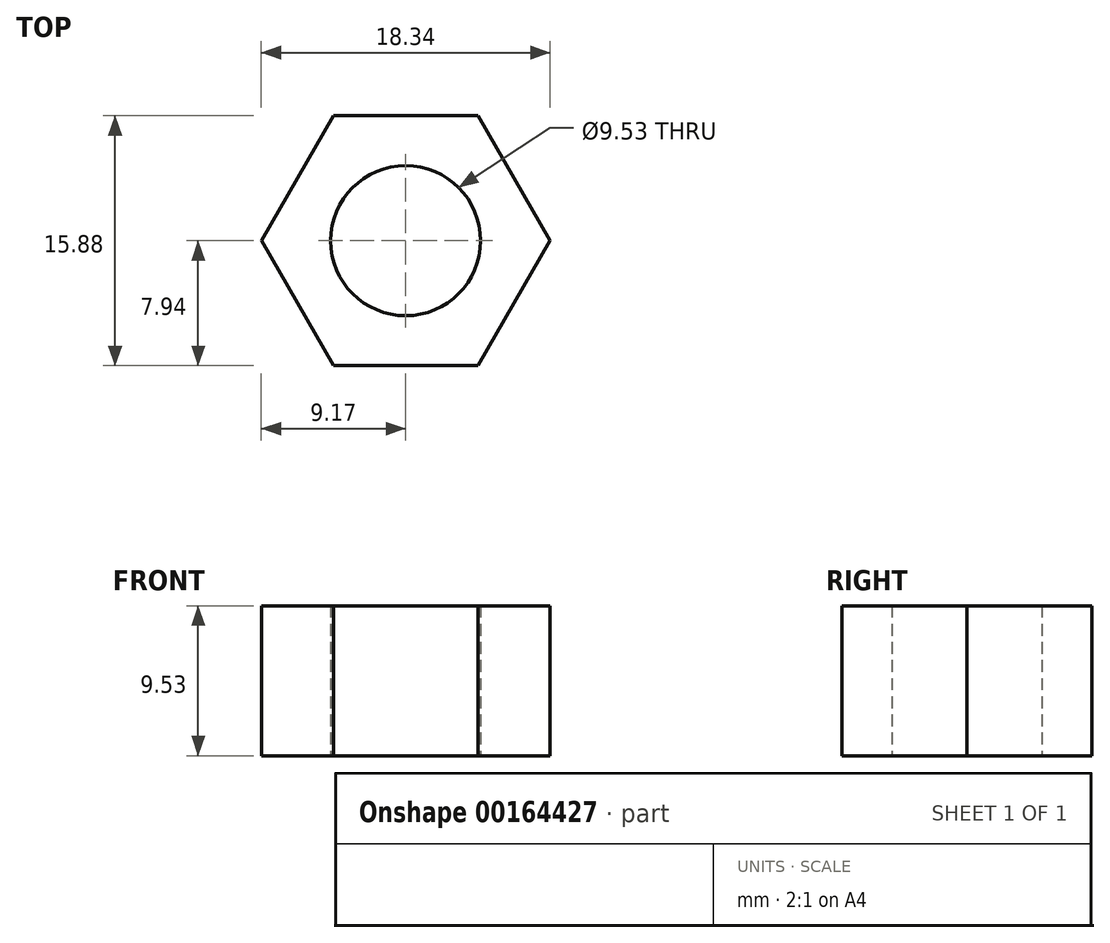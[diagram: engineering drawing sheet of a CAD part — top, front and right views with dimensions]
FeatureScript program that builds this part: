
annotation { "Feature Type Name" : "Feature", "Feature Type Description" : "" }
export const myFeature = defineFeature(function(context is Context, id is Id, definition is map)
    precondition{}
    {
        {
            var Q0;
            Q0=qCreatedBy(makeId("Top.planeOp"),FACE);
            var sketch = newSketch(context, id + "F0", { "sketchPlane" : qUnion([Q0])});
            skCircle(sketch, "E0.cCircle", {"center": v(0, 0) * mm, "radius": 7.94 * mm, "construction": true});
            skLineSegment(sketch, "E0.0", {"start": v(-4.58, -7.94) * mm, "end": v(-9.17, 0) * mm});
            skLineSegment(sketch, "E0.1", {"start": v(-9.17, 0) * mm, "end": v(-4.58, 7.94) * mm});
            skLineSegment(sketch, "E0.2", {"start": v(-4.58, 7.94) * mm, "end": v(4.58, 7.94) * mm});
            skLineSegment(sketch, "E0.3", {"start": v(4.58, 7.94) * mm, "end": v(9.17, 0) * mm});
            skLineSegment(sketch, "E0.4", {"start": v(9.17, 0) * mm, "end": v(4.58, -7.94) * mm});
            skLineSegment(sketch, "E0.5", {"start": v(4.58, -7.94) * mm, "end": v(-4.58, -7.94) * mm});
            skPoint(sketch, "E0.0.midPoint", {"position": v(-6.87, -3.97) * mm});
            skLineSegment(sketch, "E1", {"start": v(0, 0) * mm, "end": v(9.17, 0) * mm, "construction": true});
            skCircle(sketch, "E2", {"center": v(0, 0) * mm, "radius": 4.76 * mm});
            skSolve(sketch);
        }
        {
            var Q0;
            Q0=makeQuery(id+"F0.imprint","IMPRINT",FACE,{"disambiguationData":[TD([[makeQuery(id+"F0.imprint","IMPRINT",EDGE,{"derivedFrom":sQuery(id+"F0.wireOp",EDGE,"E0.0")}),-1.0]])]});
            extrude(context, id + "F1", {"entities" : qUnion([Q0]), "depth" : 9.52 * mm});
        }
    });
